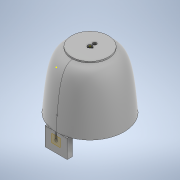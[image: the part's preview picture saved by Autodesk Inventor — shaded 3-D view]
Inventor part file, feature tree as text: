
AUTODESK INVENTOR PART (.ipt)
format: ipt  version: 2021.1 (Build 251245010, 245A)  size: 522,752 bytes
history: native  units: mm
features: sketch x12, extrude x8, plane x5, mirror x5, revolve x1, hole x1, thread x1
ambient origin geometry x8: Origin, YZ Plane, XZ Plane, XY Plane, X Axis, Y Axis, Z Axis, Center Point
bodies: Solid1 (feature_tree)
feature tree (33):
  extrude  "Extrusion1"  Depth=25.0mm
  plane  "Work Plane2"
  revolve  "Revolution1"  [1 undecoded]
  mirror  "Mirror1"
  plane  "Work Plane3"
  hole  "Hole1"  [1 undecoded]
  thread  "Thread1"  [1 undecoded]
  extrude  "Extrusion2"  Depth=10.0mm
  mirror  "Mirror2"
  extrude  "Extrusion4"  Depth=25.0mm
  sketch  "Sketch9"  dims[d36=0.0mm d40=10.0mm]
  plane  "Work Plane4"
  extrude  "Extrusion5"  Depth=55.0mm
  mirror  "Mirror4"
  extrude  "Extrusion6"  Depth=12.0mm
  sketch  "Sketch12"  dims[d46=5.0mm d49=12.0mm]
  mirror  "Mirror5"
  sketch  "Sketch13"  dims[d50=0.0mm d51=14.5mm]
  plane  "Work Plane5"
  extrude  "Extrusion7"  Depth=14.5mm
  mirror  "Mirror6"
  extrude  "Extrusion8"  Depth=1.5mm
  extrude  "Extrusion9"  Depth=14.5mm
  plane  "Work Plane1"
  sketch  "Sketch3"  dims[d3=0.0mm d4=25.0mm d5=-50.0mm]
  sketch  "Sketch4"  dims[d9=15.0mm d10=15.0mm]
  sketch  "Sketch6"  dims[d11=360.0deg d12=92.0455mm]
  sketch  "Sketch8"  dims[d16=3.0mm d17=6.0mm d18=4.0mm d19=2.0mm d20=90.0deg d21=8.0mm d22=20.594885mm d23=178.334mm d24=0.0mm]
  sketch  "Sketch10"  dims[d41=0.0mm d42=0.0mm d43=25.0mm]
  sketch  "Sketch11"  dims[d44=5.0mm d45=55.0mm]
  sketch  "Sketch14"  dims[d56=6.8mm d57=1.5mm]
  sketch  "Sketch15"  dims[d58=12.0mm d59=0.0mm d60=14.5mm]
  sketch  "Sketch16"  dims[d61=10.0mm d62=0.0mm d63=90.0deg d65=1.0mm d66=0.0mm d68=0.0mm d69=0.0mm d71=6.0mm d72=2.5mm d74=17.0mm d75=0.0mm]
note: 3 required parameter values undecoded (feature->parameter linkage not recoverable at this tier; creation-order binding heuristic only, values carry confidence <= 0.55)